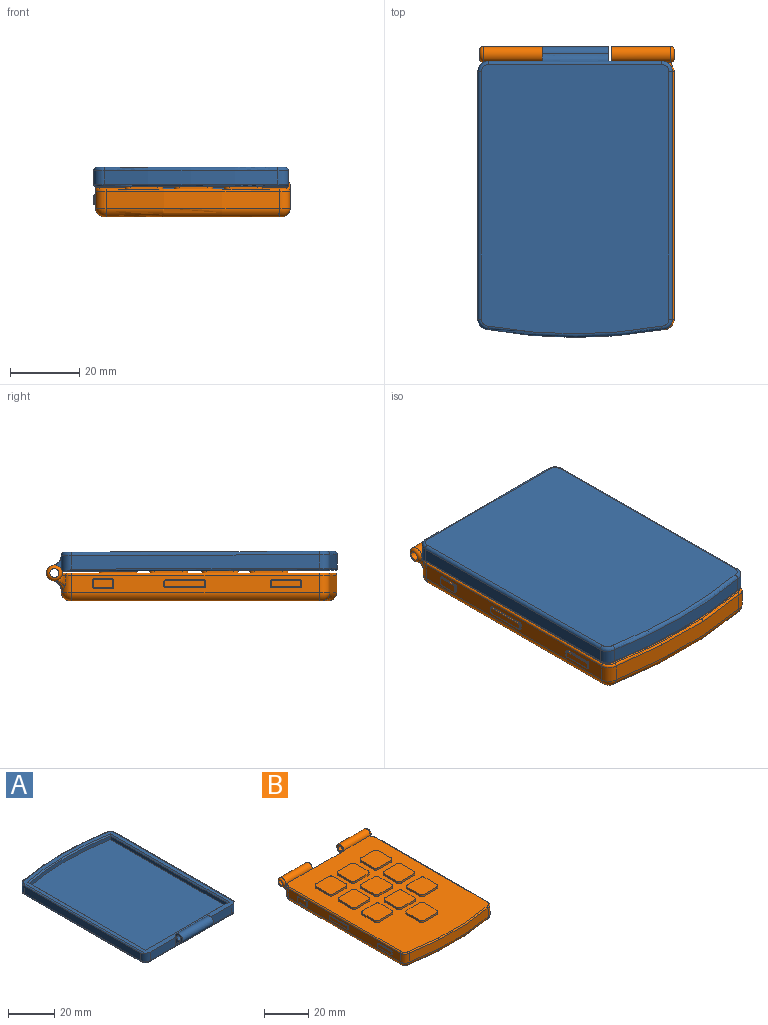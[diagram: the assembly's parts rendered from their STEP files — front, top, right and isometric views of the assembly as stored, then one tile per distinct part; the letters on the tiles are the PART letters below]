
ASSEMBLY  parts=2 mates=1
PART A: 37 faces, bbox 56.6x86.1x8.3 mm
  f0: cylinder r=1.3mm len=19mm, axis (-1,0,0), area 155.2mm2, adj f2,f3
  f1: cylinder r=2.25mm len=19mm, axis (-1,0,0), area 204.2mm2, adj f2,f3,f4,f19
  f2: plane 7.3x4.56mm, normal (1,0,0), area 12.8mm2, adj f0,f1,f4,f5,f19
  f3: plane 7.3x4.56mm, normal (-1,0,0), area 12.8mm2, adj f0,f1,f4,f5,f19
  f4: plane 78.92x54.8mm, normal (0,0,1), area 483.8mm2, adj f1,f2,f3,f5,f6,f12,f28,f29
  f5: plane 50x4.5mm, normal (0,-1,0), area 139.8mm2, adj f2,f3,f4,f6,f12,f19,f23
  f6: cylinder r=3mm len=4.5mm, axis (0,0,1), area 20.8mm2, adj f4,f5,f7,f21,f28
  f7: plane 71.26x3.9mm, normal (1,0,0), area 277.9mm2, adj f6,f8,f20,f28
  f8: cylinder r=3mm len=3.9mm, axis (0,0,1), area 18.4mm2, adj f7,f9,f22,f29
  f9: cylinder r=140mm len=50mm, axis (0,0,1), area 196.1mm2, adj f8,f10,f24,f30
  f10: cylinder r=3mm len=3.9mm, axis (0,0,1), area 18.4mm2, adj f9,f11,f26,f31
  f11: plane 71.26x3.9mm, normal (-1,0,0), area 277.9mm2, adj f10,f12,f27,f32
  f12: cylinder r=3mm len=4.5mm, axis (0,0,1), area 20.8mm2, adj f4,f5,f11,f25,f32
  f13: plane 77.52x54mm, normal (0,0,-1), area 4135.7mm2, adj f20,f21,f22,f23,f24,f25,f26,f27
  f14: plane 50x1.9mm, normal (0,1,0), area 95mm2, adj f15,f17,f18,f36
  f15: plane 71.21x1.9mm, normal (-1,0,0), area 135.3mm2, adj f14,f16,f18,f34
  f16: cylinder r=137mm len=50mm, axis (0,0,1), area 95.5mm2, adj f15,f17,f18,f33
  f17: plane 71.21x1.9mm, normal (1,0,0), area 135.3mm2, adj f14,f16,f18,f35
  f18: plane 73.52x50mm, normal (0,0,1), area 3637.5mm2, adj f14,f15,f16,f17
  f19: bspline ~43.77x2.76mm, area 75.1mm2, adj f1,f2,f3,f5
  f20: cylinder r=1mm len=71.26mm, axis (0,-1,0), area 111.9mm2, adj f7,f13,f21,f22
  f21: torus R=2mm, axis (0,0,1), area 6.5mm2, adj f6,f13,f20,f23
  f22: torus R=2mm, axis (0,0,1), area 6.6mm2, adj f8,f13,f20,f24
  f23: cylinder r=1mm len=50mm, axis (-1,0,0), area 78.5mm2, adj f5,f13,f21,f25
  f24: torus R=139mm, axis (0,0,1), area 78.9mm2, adj f9,f13,f22,f26
  f25: torus R=2mm, axis (0,0,1), area 6.5mm2, adj f12,f13,f23,f27
  f26: torus R=2mm, axis (0,0,1), area 6.6mm2, adj f10,f13,f24,f27
  f27: cylinder r=1mm len=71.26mm, axis (0,1,0), area 111.9mm2, adj f11,f13,f25,f26
  f28: cylinder r=0.6mm len=73.06mm, axis (0,1,0), area 68mm2, adj f4,f6,f7,f29
  f29: torus R=2.4mm, axis (0,0,1), area 4.1mm2, adj f4,f8,f28,f30
  f30: torus R=139.4mm, axis (0,0,1), area 47.4mm2, adj f4,f9,f29,f31
  f31: torus R=2.4mm, axis (0,0,1), area 4.1mm2, adj f4,f10,f30,f32
  f32: cylinder r=0.6mm len=73.06mm, axis (0,-1,0), area 68mm2, adj f4,f11,f12,f31
  f33: cone r=137mm half-angle=45deg, axis (0,0,1), area 43.2mm2, adj f4,f16,f34,f35
  f34: plane 72.31x0.6mm, normal (-0.71,0,0.71), area 60.9mm2, adj f4,f15,f33,f36
  f35: plane 72.31x0.6mm, normal (0.71,0,0.71), area 60.9mm2, adj f4,f17,f33,f36
  f36: plane 51.2x0.6mm, normal (0,0.71,0.71), area 42.9mm2, adj f4,f14,f34,f35
PART B: 204 faces, bbox 106.1x86.4x10.5 mm
  f0: plane 71.26x4.9mm, normal (1,0,0), area 334.7mm2, adj f12,f18,f121,f126,f193,f194,f195,f196
  f1: bspline ~3.29x3.07mm, area 3.4mm2, adj f10,f12,f114,f115
  f2: bspline ~3.29x3.07mm, area 3.4mm2, adj f6,f14,f111,f112
  f3: cylinder r=1.3mm len=18mm, axis (-1,0,0), area 147mm2, adj f5,f6
  f4: cylinder r=2.25mm len=17mm, axis (-1,0,0), area 164.5mm2, adj f5,f6,f11,f110,f112,f132,f139,f140
  f5: plane 7.47x4.56mm, normal (1,0,0), area 12.8mm2, adj f3,f4,f11,f13,f110,f139,f140
  f6: torus R=1.25mm, axis (-1,0,0), area 18.2mm2, adj f2,f3,f4,f111
  f7: cylinder r=1.3mm len=18mm, axis (1,0,0), area 147mm2, adj f9,f10
  f8: cylinder r=2.25mm len=17mm, axis (1,0,0), area 164.5mm2, adj f9,f10,f11,f113,f114,f124,f136,f137
  f9: plane 7.47x4.56mm, normal (-1,0,0), area 12.8mm2, adj f7,f8,f11,f13,f113,f136,f137
  f10: torus R=1.25mm, axis (1,0,0), area 18.2mm2, adj f1,f7,f8,f115
  f11: plane 78.92x54.8mm, normal (0,0,1), area 3078.8mm2, adj f4,f5,f8,f9,f13,f20,f21,f22
  f12: cylinder r=3mm len=4.9mm, axis (0,0,1), area 11mm2, adj f0,f1,f13,f114,f115,f119,f125
  f13: plane 50x5.5mm, normal (0,1,0), area 93.5mm2, adj f5,f9,f11,f12,f14,f110,f113,f117
  f14: cylinder r=3mm len=4.9mm, axis (0,0,1), area 11mm2, adj f2,f13,f15,f111,f112,f116,f131
  f15: plane 71.26x4.9mm, normal (-1,0,0), area 286.8mm2, adj f14,f16,f118,f130,f142,f143,f144,f145
  f16: cylinder r=3mm len=4.9mm, axis (0,0,1), area 23.1mm2, adj f15,f17,f120,f129
  f17: cylinder r=140mm len=50mm, axis (0,0,1), area 246.3mm2, adj f16,f18,f122,f128
  f18: cylinder r=3mm len=4.9mm, axis (0,0,1), area 23.1mm2, adj f0,f17,f123,f127
  f19: plane 74.52x51mm, normal (0,0,-1), area 3759.7mm2, adj f116,f117,f118,f119,f120,f121,f122,f123
  f20: plane 8x1mm, normal (1,0,0), area 8mm2, adj f11,f24,f106,f109
  f21: plane 8x1mm, normal (0,1,0), area 8mm2, adj f11,f24,f108,f109
  f22: plane 8x1mm, normal (-1,0,0), area 8mm2, adj f11,f24,f107,f108
  f23: plane 8x1mm, normal (0,-1,0), area 8mm2, adj f11,f24,f106,f107
  f24: plane 11x11mm, normal (0,0,1), area 119.1mm2, adj f20,f21,f22,f23,f106,f107,f108,f109
  f25: plane 8x1mm, normal (0,1,0), area 8mm2, adj f11,f29,f102,f105
  f26: plane 8x1mm, normal (-1,0,0), area 8mm2, adj f11,f29,f102,f103
  f27: plane 8x1mm, normal (0,-1,0), area 8mm2, adj f11,f29,f103,f104
  f28: plane 8x1mm, normal (1,0,0), area 8mm2, adj f11,f29,f104,f105
  f29: plane 11x11mm, normal (0,0,1), area 119.1mm2, adj f25,f26,f27,f28,f102,f103,f104,f105
  f30: plane 8x1mm, normal (0,-1,0), area 8mm2, adj f11,f34,f98,f101
  f31: plane 8x1mm, normal (1,0,0), area 8mm2, adj f11,f34,f100,f101
  f32: plane 8x1mm, normal (0,1,0), area 8mm2, adj f11,f34,f99,f100
  f33: plane 8x1mm, normal (-1,0,0), area 8mm2, adj f11,f34,f98,f99
  f34: plane 11x11mm, normal (0,0,1), area 119.1mm2, adj f30,f31,f32,f33,f98,f99,f100,f101
  f35: plane 8x1mm, normal (0,1,0), area 8mm2, adj f11,f39,f90,f93
  f36: plane 8x1mm, normal (-1,0,0), area 8mm2, adj f11,f39,f92,f93
  f37: plane 8x1mm, normal (0,-1,0), area 8mm2, adj f11,f39,f91,f92
  f38: plane 8x1mm, normal (1,0,0), area 8mm2, adj f11,f39,f90,f91
  f39: plane 11x11mm, normal (0,0,1), area 119.1mm2, adj f35,f36,f37,f38,f90,f91,f92,f93
  f40: plane 8x1mm, normal (0,1,0), area 8mm2, adj f11,f44,f86,f89
  f41: plane 7.53x1mm, normal (-1,0,0), area 7.5mm2, adj f11,f44,f88,f89
  f42: plane 8x1mm, normal (0,-1,0), area 8mm2, adj f11,f44,f87,f88
  f43: plane 7.53x1mm, normal (1,0,0), area 7.5mm2, adj f11,f44,f86,f87
  f44: plane 11x10.53mm, normal (0,0,1), area 113.9mm2, adj f40,f41,f42,f43,f86,f87,f88,f89
  f45: plane 7.53x1mm, normal (-1,0,0), area 7.5mm2, adj f11,f49,f78,f81
  f46: plane 8x1mm, normal (0,-1,0), area 8mm2, adj f11,f49,f80,f81
  f47: plane 7.53x1mm, normal (1,0,0), area 7.5mm2, adj f11,f49,f79,f80
  f48: plane 8x1mm, normal (0,1,0), area 8mm2, adj f11,f49,f78,f79
  f49: plane 11x10.53mm, normal (0,0,1), area 113.9mm2, adj f45,f46,f47,f48,f78,f79,f80,f81
  f50: plane 8x1mm, normal (-1,0,0), area 8mm2, adj f11,f54,f94,f97
  f51: plane 8x1mm, normal (0,-1,0), area 8mm2, adj f11,f54,f96,f97
  f52: plane 8x1mm, normal (1,0,0), area 8mm2, adj f11,f54,f95,f96
  f53: plane 8x1mm, normal (0,1,0), area 8mm2, adj f11,f54,f94,f95
  f54: plane 11x11mm, normal (0,0,1), area 119.1mm2, adj f50,f51,f52,f53,f94,f95,f96,f97
  f55: plane 8x1mm, normal (0,1,0), area 8mm2, adj f11,f59,f82,f85
  f56: plane 7.53x1mm, normal (-1,0,0), area 7.5mm2, adj f11,f59,f84,f85
  f57: plane 8x1mm, normal (0,-1,0), area 8mm2, adj f11,f59,f83,f84
  f58: plane 7.53x1mm, normal (1,0,0), area 7.5mm2, adj f11,f59,f82,f83
  f59: plane 11x10.53mm, normal (0,0,1), area 113.9mm2, adj f55,f56,f57,f58,f82,f83,f84,f85
  f60: plane 8x1mm, normal (0,1,0), area 8mm2, adj f11,f64,f74,f77
  f61: plane 8x1mm, normal (-1,0,0), area 8mm2, adj f11,f64,f74,f75
  f62: plane 8x1mm, normal (0,-1,0), area 8mm2, adj f11,f64,f75,f76
  f63: plane 8x1mm, normal (1,0,0), area 8mm2, adj f11,f64,f76,f77
  f64: plane 11x11mm, normal (0,0,1), area 119.1mm2, adj f60,f61,f62,f63,f74,f75,f76,f77
  f65: plane 8x1mm, normal (0,-1,0), area 8mm2, adj f11,f69,f70,f73
  f66: plane 8x1mm, normal (1,0,0), area 8mm2, adj f11,f69,f70,f71
  f67: plane 8x1mm, normal (0,1,0), area 8mm2, adj f11,f69,f71,f72
  f68: plane 8x1mm, normal (-1,0,0), area 8mm2, adj f11,f69,f72,f73
  f69: plane 11x11mm, normal (0,0,1), area 119.1mm2, adj f65,f66,f67,f68,f70,f71,f72,f73
  f70: cylinder r=1.5mm len=1.5mm, axis (0,0,1), area 2.4mm2, adj f11,f65,f66,f69
  f71: cylinder r=1.5mm len=1.5mm, axis (0,0,-1), area 2.4mm2, adj f11,f66,f67,f69
  f72: cylinder r=1.5mm len=1.5mm, axis (0,0,1), area 2.4mm2, adj f11,f67,f68,f69
  f73: cylinder r=1.5mm len=1.5mm, axis (0,0,-1), area 2.4mm2, adj f11,f65,f68,f69
  f74: cylinder r=1.5mm len=1.5mm, axis (0,0,1), area 2.4mm2, adj f11,f60,f61,f64
  f75: cylinder r=1.5mm len=1.5mm, axis (0,0,-1), area 2.4mm2, adj f11,f61,f62,f64
  f76: cylinder r=1.5mm len=1.5mm, axis (0,0,1), area 2.4mm2, adj f11,f62,f63,f64
  f77: cylinder r=1.5mm len=1.5mm, axis (0,0,-1), area 2.4mm2, adj f11,f60,f63,f64
  f78: cylinder r=1.5mm len=1.5mm, axis (0,0,-1), area 2.4mm2, adj f11,f45,f48,f49
  f79: cylinder r=1.5mm len=1.5mm, axis (0,0,-1), area 2.4mm2, adj f11,f47,f48,f49
  f80: cylinder r=1.5mm len=1.5mm, axis (0,0,1), area 2.4mm2, adj f11,f46,f47,f49
  f81: cylinder r=1.5mm len=1.5mm, axis (0,0,1), area 2.4mm2, adj f11,f45,f46,f49
  f82: cylinder r=1.5mm len=1.5mm, axis (0,0,-1), area 2.4mm2, adj f11,f55,f58,f59
  f83: cylinder r=1.5mm len=1.5mm, axis (0,0,1), area 2.4mm2, adj f11,f57,f58,f59
  f84: cylinder r=1.5mm len=1.5mm, axis (0,0,-1), area 2.4mm2, adj f11,f56,f57,f59
  f85: cylinder r=1.5mm len=1.5mm, axis (0,0,1), area 2.4mm2, adj f11,f55,f56,f59
  f86: cylinder r=1.5mm len=1.5mm, axis (0,0,1), area 2.4mm2, adj f11,f40,f43,f44
  f87: cylinder r=1.5mm len=1.5mm, axis (0,0,-1), area 2.4mm2, adj f11,f42,f43,f44
  f88: cylinder r=1.5mm len=1.5mm, axis (0,0,-1), area 2.4mm2, adj f11,f41,f42,f44
  f89: cylinder r=1.5mm len=1.5mm, axis (0,0,1), area 2.4mm2, adj f11,f40,f41,f44
  f90: cylinder r=1.5mm len=1.5mm, axis (0,0,1), area 2.4mm2, adj f11,f35,f38,f39
  f91: cylinder r=1.5mm len=1.5mm, axis (0,0,-1), area 2.4mm2, adj f11,f37,f38,f39
  f92: cylinder r=1.5mm len=1.5mm, axis (0,0,-1), area 2.4mm2, adj f11,f36,f37,f39
  f93: cylinder r=1.5mm len=1.5mm, axis (0,0,1), area 2.4mm2, adj f11,f35,f36,f39
  f94: cylinder r=1.5mm len=1.5mm, axis (0,0,1), area 2.4mm2, adj f11,f50,f53,f54
  f95: cylinder r=1.5mm len=1.5mm, axis (0,0,1), area 2.4mm2, adj f11,f52,f53,f54
  f96: cylinder r=1.5mm len=1.5mm, axis (0,0,1), area 2.4mm2, adj f11,f51,f52,f54
  f97: cylinder r=1.5mm len=1.5mm, axis (0,0,1), area 2.4mm2, adj f11,f50,f51,f54
  f98: cylinder r=1.5mm len=1.5mm, axis (0,0,1), area 2.4mm2, adj f11,f30,f33,f34
  f99: cylinder r=1.5mm len=1.5mm, axis (0,0,-1), area 2.4mm2, adj f11,f32,f33,f34
  f100: cylinder r=1.5mm len=1.5mm, axis (0,0,-1), area 2.4mm2, adj f11,f31,f32,f34
  f101: cylinder r=1.5mm len=1.5mm, axis (0,0,1), area 2.4mm2, adj f11,f30,f31,f34
  f102: cylinder r=1.5mm len=1.5mm, axis (0,0,-1), area 2.4mm2, adj f11,f25,f26,f29
  f103: cylinder r=1.5mm len=1.5mm, axis (0,0,-1), area 2.4mm2, adj f11,f26,f27,f29
  f104: cylinder r=1.5mm len=1.5mm, axis (0,0,1), area 2.4mm2, adj f11,f27,f28,f29
  f105: cylinder r=1.5mm len=1.5mm, axis (0,0,1), area 2.4mm2, adj f11,f25,f28,f29
  f106: cylinder r=1.5mm len=1.5mm, axis (0,0,1), area 2.4mm2, adj f11,f20,f23,f24
  f107: cylinder r=1.5mm len=1.5mm, axis (0,0,1), area 2.4mm2, adj f11,f22,f23,f24
  f108: cylinder r=1.5mm len=1.5mm, axis (0,0,1), area 2.4mm2, adj f11,f21,f22,f24
  f109: cylinder r=1.5mm len=1.5mm, axis (0,0,1), area 2.4mm2, adj f11,f20,f21,f24
  f110: bspline ~66.5x2.95mm, area 62.1mm2, adj f4,f5,f13,f112
  f111: bspline ~3.37x2.76mm, area 5mm2, adj f2,f6,f14,f132
  f112: bspline ~4.19x3.04mm, area 5.9mm2, adj f2,f4,f14,f110
  f113: bspline ~66.5x2.95mm, area 62.1mm2, adj f8,f9,f13,f114
  f114: bspline ~4.19x3.04mm, area 5.9mm2, adj f1,f8,f12,f113
  f115: bspline ~3.37x2.76mm, area 5mm2, adj f1,f10,f12,f124
  f116: torus R=0.5mm, axis (0,0,1), area 12.9mm2, adj f14,f19,f117,f118
  f117: cylinder r=2.5mm len=50mm, axis (1,0,0), area 196.3mm2, adj f13,f19,f116,f119
  f118: cylinder r=2.5mm len=71.26mm, axis (0,1,0), area 279.9mm2, adj f15,f19,f116,f120
  f119: torus R=0.5mm, axis (0,0,1), area 12.9mm2, adj f12,f19,f117,f121
  f120: torus R=0.5mm, axis (0,0,1), area 13.8mm2, adj f16,f19,f118,f122
  f121: cylinder r=2.5mm len=71.26mm, axis (0,-1,0), area 279.9mm2, adj f0,f19,f119,f123
  f122: torus R=137.5mm, axis (0,0,1), area 197.4mm2, adj f17,f19,f120,f123
  f123: torus R=0.5mm, axis (0,0,1), area 13.8mm2, adj f18,f19,f121,f122
  f124: bspline ~2.57x1.6mm, area 1.2mm2, adj f8,f11,f115,f125
  f125: torus R=2.4mm, axis (0,0,1), area 1.6mm2, adj f11,f12,f124,f126
  f126: cylinder r=0.6mm len=71.26mm, axis (0,1,0), area 67.2mm2, adj f0,f11,f125,f127
  f127: torus R=2.4mm, axis (0,0,1), area 4.1mm2, adj f11,f18,f126,f128
  f128: torus R=139.4mm, axis (0,0,1), area 47.4mm2, adj f11,f17,f127,f129
  f129: torus R=2.4mm, axis (0,0,1), area 4.1mm2, adj f11,f16,f128,f130
  f130: cylinder r=0.6mm len=71.26mm, axis (0,-1,0), area 67.2mm2, adj f11,f15,f129,f131
  f131: torus R=2.4mm, axis (0,0,1), area 1.6mm2, adj f11,f14,f130,f132
  f132: bspline ~2.58x1.59mm, area 1.2mm2, adj f4,f11,f111,f131
  f133: plane 1.42x0.45mm, normal (1,0,0), area 0.4mm2, adj f11,f13,f135
  f134: plane 1.42x0.45mm, normal (-1,0,0), area 0.4mm2, adj f11,f13,f135
  f135: cylinder r=2.45mm len=19mm, axis (-1,0,0), area 28.7mm2, adj f11,f13,f133,f134
  f136: plane 15x0.53mm, normal (0,1,0), area 8mm2, adj f8,f9,f137,f138
  f137: plane 16.06x0.19mm, normal (0,0,-1), area 3mm2, adj f8,f9,f136,f138
  f138: cylinder r=3mm len=1.06mm, axis (0,0,1), area 0.3mm2, adj f8,f136,f137
  f139: plane 16.06x0.19mm, normal (0,0,-1), area 3mm2, adj f4,f5,f140,f141
  f140: plane 15x0.53mm, normal (0,1,0), area 8mm2, adj f4,f5,f139,f141
  f141: cylinder r=3mm len=1.06mm, axis (0,0,1), area 0.3mm2, adj f4,f139,f140
  f142: plane 5x0.3mm, normal (0,0,-1), area 1.5mm2, adj f15,f165,f168,f175
  f143: plane 1.8x0.3mm, normal (0,-1,0), area 0.5mm2, adj f15,f167,f168,f171
  f144: plane 5x0.3mm, normal (0,0,1), area 1.5mm2, adj f15,f166,f167,f170
  f145: plane 1.8x0.3mm, normal (0,1,0), area 0.5mm2, adj f15,f165,f166,f174
  f146: plane 5.6x2.4mm, normal (-1,0,0), area 13.4mm2, adj f169,f170,f171,f172,f173,f174,f175,f176
  f147: plane 8x0.3mm, normal (0,0,-1), area 2.4mm2, adj f15,f161,f164,f182
  f148: plane 1.2x0.3mm, normal (0,-1,0), area 0.4mm2, adj f15,f161,f162,f183
  f149: plane 8x0.3mm, normal (0,0,1), area 2.4mm2, adj f15,f162,f163,f179
  f150: plane 1.2x0.3mm, normal (0,1,0), area 0.4mm2, adj f15,f163,f164,f178
  f151: plane 8.6x1.8mm, normal (-1,0,0), area 15.4mm2, adj f177,f178,f179,f180,f181,f182,f183,f184
  f152: plane 11x0.3mm, normal (0,0,-1), area 3.3mm2, adj f15,f157,f160,f191
  f153: plane 1.2x0.3mm, normal (0,-1,0), area 0.4mm2, adj f15,f159,f160,f187
  f154: plane 11x0.3mm, normal (0,0,1), area 3.3mm2, adj f15,f158,f159,f186
  f155: plane 1.2x0.3mm, normal (0,1,0), area 0.4mm2, adj f15,f157,f158,f190
  f156: plane 11.6x1.8mm, normal (-1,0,0), area 20.8mm2, adj f185,f186,f187,f188,f189,f190,f191,f192
  f157: cylinder r=0.5mm len=0.5mm, axis (1,0,0), area 0.2mm2, adj f15,f152,f155,f192
  f158: cylinder r=0.5mm len=0.5mm, axis (-1,0,0), area 0.2mm2, adj f15,f154,f155,f188
  f159: cylinder r=0.5mm len=0.5mm, axis (1,0,0), area 0.2mm2, adj f15,f153,f154,f185
  f160: cylinder r=0.5mm len=0.5mm, axis (-1,0,0), area 0.2mm2, adj f15,f152,f153,f189
  f161: cylinder r=0.5mm len=0.5mm, axis (-1,0,0), area 0.2mm2, adj f15,f147,f148,f184
  f162: cylinder r=0.5mm len=0.5mm, axis (1,0,0), area 0.2mm2, adj f15,f148,f149,f181
  f163: cylinder r=0.5mm len=0.5mm, axis (-1,0,0), area 0.2mm2, adj f15,f149,f150,f177
  f164: cylinder r=0.5mm len=0.5mm, axis (1,0,0), area 0.2mm2, adj f15,f147,f150,f180
  f165: cylinder r=0.5mm len=0.5mm, axis (1,0,0), area 0.2mm2, adj f15,f142,f145,f176
  f166: cylinder r=0.5mm len=0.5mm, axis (-1,0,0), area 0.2mm2, adj f15,f144,f145,f172
  f167: cylinder r=0.5mm len=0.5mm, axis (1,0,0), area 0.2mm2, adj f15,f143,f144,f169
  f168: cylinder r=0.5mm len=0.5mm, axis (-1,0,0), area 0.2mm2, adj f15,f142,f143,f173
  f169: torus R=0.3mm, axis (-1,0,0), area 0.2mm2, adj f146,f167,f170,f171
  f170: cylinder r=0.2mm len=5mm, axis (0,-1,0), area 1.6mm2, adj f144,f146,f169,f172
  f171: cylinder r=0.2mm len=1.8mm, axis (0,0,-1), area 0.6mm2, adj f143,f146,f169,f173
  f172: torus R=0.3mm, axis (-1,0,0), area 0.2mm2, adj f146,f166,f170,f174
  f173: torus R=0.3mm, axis (-1,0,0), area 0.2mm2, adj f146,f168,f171,f175
  f174: cylinder r=0.2mm len=1.8mm, axis (0,0,1), area 0.6mm2, adj f145,f146,f172,f176
  f175: cylinder r=0.2mm len=5mm, axis (0,1,0), area 1.6mm2, adj f142,f146,f173,f176
  f176: torus R=0.3mm, axis (-1,0,0), area 0.2mm2, adj f146,f165,f174,f175
  f177: torus R=0.3mm, axis (-1,0,0), area 0.2mm2, adj f151,f163,f178,f179
  f178: cylinder r=0.2mm len=1.2mm, axis (0,0,1), area 0.4mm2, adj f150,f151,f177,f180
  f179: cylinder r=0.2mm len=8mm, axis (0,-1,0), area 2.5mm2, adj f149,f151,f177,f181
  f180: torus R=0.3mm, axis (-1,0,0), area 0.2mm2, adj f151,f164,f178,f182
  f181: torus R=0.3mm, axis (-1,0,0), area 0.2mm2, adj f151,f162,f179,f183
  f182: cylinder r=0.2mm len=8mm, axis (0,1,0), area 2.5mm2, adj f147,f151,f180,f184
  f183: cylinder r=0.2mm len=1.2mm, axis (0,0,-1), area 0.4mm2, adj f148,f151,f181,f184
  f184: torus R=0.3mm, axis (-1,0,0), area 0.2mm2, adj f151,f161,f182,f183
  f185: torus R=0.3mm, axis (-1,0,0), area 0.2mm2, adj f156,f159,f186,f187
  f186: cylinder r=0.2mm len=11mm, axis (0,-1,0), area 3.5mm2, adj f154,f156,f185,f188
  f187: cylinder r=0.2mm len=1.2mm, axis (0,0,-1), area 0.4mm2, adj f153,f156,f185,f189
  f188: torus R=0.3mm, axis (-1,0,0), area 0.2mm2, adj f156,f158,f186,f190
  f189: torus R=0.3mm, axis (-1,0,0), area 0.2mm2, adj f156,f160,f187,f191
  f190: cylinder r=0.2mm len=1.2mm, axis (0,0,1), area 0.4mm2, adj f155,f156,f188,f192
  f191: cylinder r=0.2mm len=11mm, axis (0,1,0), area 3.5mm2, adj f152,f156,f189,f192
  f192: torus R=0.3mm, axis (-1,0,0), area 0.2mm2, adj f156,f157,f190,f191
  f193: plane 6.5x5.77mm, normal (0,0,-1), area 37.5mm2, adj f0,f194,f202,f203
  f194: cylinder r=0.3mm len=6.5mm, axis (1,0,0), area 2.4mm2, adj f0,f193,f195,f203
  f195: plane 6.5x0.95mm, normal (0,0.94,-0.33), area 6.5mm2, adj f0,f194,f196,f203
  f196: plane 6.5x0.7mm, normal (0,1,0), area 4.5mm2, adj f0,f195,f197,f203
  f197: cylinder r=0.3mm len=6.5mm, axis (1,0,0), area 3.1mm2, adj f0,f196,f198,f203
  f198: plane 6.5x6.4mm, normal (0,0,1), area 41.6mm2, adj f0,f197,f199,f203
  f199: cylinder r=0.3mm len=6.5mm, axis (1,0,0), area 3.1mm2, adj f0,f198,f200,f203
  f200: plane 6.5x0.7mm, normal (0,-1,0), area 4.5mm2, adj f0,f199,f201,f203
  f201: plane 6.5x0.95mm, normal (0,-0.94,-0.33), area 6.5mm2, adj f0,f200,f202,f203
  f202: cylinder r=0.3mm len=6.5mm, axis (1,0,0), area 2.4mm2, adj f0,f193,f201,f203
  f203: plane 7x2.15mm, normal (1,0,0), area 14.5mm2, adj f193,f194,f195,f196,f197,f198,f199,f200
PLACE A rot(axis=(1,0,0),179.8deg) t=(0,-82.53,0.16)mm
PLACE B t=(0.5,0,0)mm fixed
MATE revolute B.f10 <-> A.f0  axis (1,0,0) through (-9.5,-41.26,0)mm
